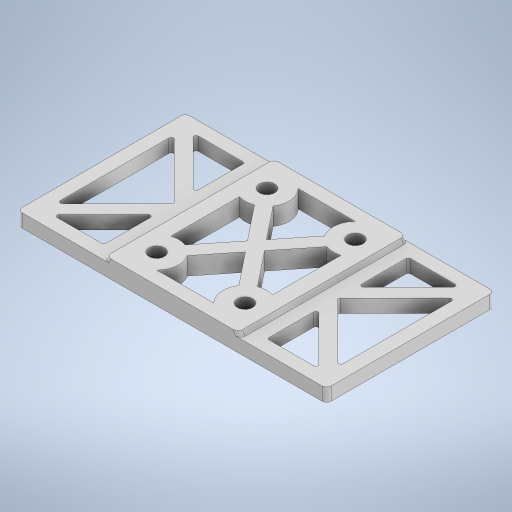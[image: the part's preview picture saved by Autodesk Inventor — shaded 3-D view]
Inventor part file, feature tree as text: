
AUTODESK INVENTOR PART (.ipt)
format: ipt  version: 2024.2 (Build 282272000, 272)  size: 457,728 bytes
history: native  units: mm
features: sketch x7, extrude x6, fillet x3, chamfer x2, hole x1
ambient origin geometry x8: Origin, YZ Plane, XZ Plane, XY Plane, X Axis, Y Axis, Z Axis, Center Point
bodies: Solid1 (feature_tree)
feature tree (19):
  extrude  "Extrusion1"  Depth=38.0mm
  extrude  "Extrusion2"  Depth=1.0mm
  chamfer  "Chamfer2"  Distance=1.0mm
  chamfer  "Chamfer3"  Distance=1.0mm Angle=30.0deg
  extrude  "Extrusion3"  Depth=1.0mm
  fillet  "Fillet1"  Radius=3.0mm
  fillet  "Fillet4"  Radius=3.0mm
  hole  "Hole1"  [1 undecoded]
  extrude  "Extrusion6"  TaperAngle=0.0deg  [1 undecoded]
  fillet  "Fillet3"  Radius=0.5mm
  extrude  "Extrusion4"  Depth=0.5mm
  extrude  "Extrusion5"  Depth=3.0mm
  sketch  "Sketch1"  dims[d0=70.0mm d1=38.0mm]
  sketch  "Sketch2"  dims[d2=3.0mm d3=0.0mm d4=31.0mm d5=1.0mm d6=0.0mm d10=1.0mm d11=2.0mm d12=30.0deg]
  sketch  "Sketch3"  dims[d13=1.0mm d14=2.0mm d15=30.0deg d16=1.0mm d19=3.0mm d20=3.0mm]
  sketch  "Sketch4"  dims[d21=3.0mm d22=3.0mm]
  sketch  "Sketch5"  dims[d24=3.0mm d25=0.0mm d26=0.0mm d27=0.5mm]
  sketch  "Sketch6"  dims[d28=0.5mm d29=3.5mm]
  sketch  "Sketch7"  dims[d30=20.0mm d31=25.0mm d32=45.0mm d33=31.5mm d34=3.5mm d35=6.0mm d36=5.25mm d37=1.0mm d38=90.0deg d39=8.0mm d40=20.594885mm d41=5.6mm d42=2.5mm d43=0.0mm d44=0.2mm d45=0.0mm d46=10.0mm d47=3.0mm d48=3.0mm d49=7.0mm d50=7.0mm d51=3.0mm d52=3.0mm d53=1.5mm d55=1.5mm d56=1.5mm d58=1.5mm d59=0.0mm d60=0.0mm]
note: 2 required parameter values undecoded (feature->parameter linkage not recoverable at this tier; creation-order binding heuristic only, values carry confidence <= 0.55)
